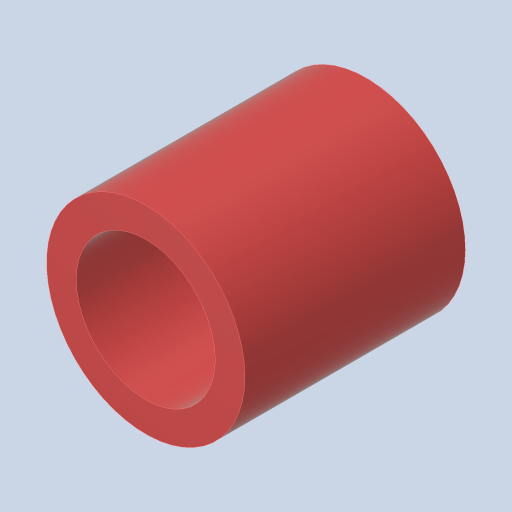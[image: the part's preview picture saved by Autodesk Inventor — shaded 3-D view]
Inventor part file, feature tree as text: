
AUTODESK INVENTOR PART (.ipt)
format: ipt  version: 2023.4 (Build 274418000, 418)  size: 120,320 bytes
history: native  units: in
note: dims shown in document units (in); Inventor stores cm internally (conversion verified against a paired STEP export)
features: extrude x1, sketch x1
ambient origin geometry x8: Origin, YZ Plane, XZ Plane, XY Plane, X Axis, Y Axis, Z Axis, Center Point
bodies: Solid1 (feature_tree)
feature tree (2):
  extrude  "Extrusion1"  Depth=0.928in
  sketch  "Sketch1"  dims[d0=0.585in d1=0.125in d2=0.928in d3=0.0in]
